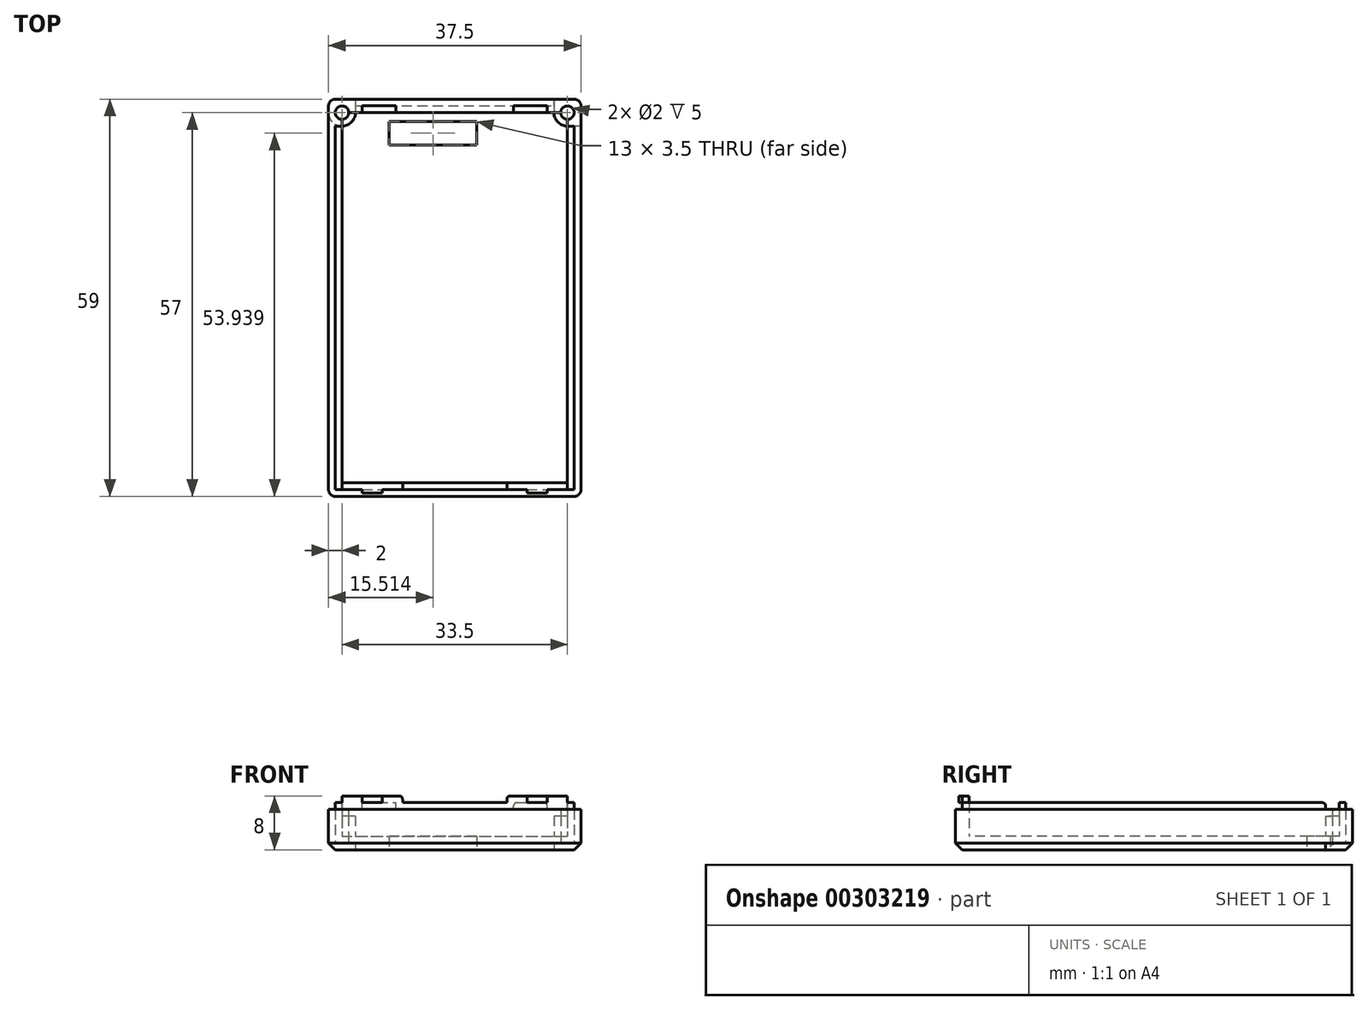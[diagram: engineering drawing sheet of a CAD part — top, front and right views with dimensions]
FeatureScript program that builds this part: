
annotation { "Feature Type Name" : "Feature", "Feature Type Description" : "" }
export const myFeature = defineFeature(function(context is Context, id is Id, definition is map)
    precondition{}
    {
        {
            var Q0;
            Q0=qCreatedBy(makeId("Top.planeOp"),FACE);
            var sketch = newSketch(context, id + "F0", { "sketchPlane" : qUnion([Q0])});
            skLineSegment(sketch, "E0.left", {"start": v(-18.5, 29.5) * mm, "end": v(-18.5, -29.5) * mm});
            skLineSegment(sketch, "E0.right", {"start": v(19, 29.5) * mm, "end": v(19, -29.5) * mm});
            skLineSegment(sketch, "E1", {"start": v(-18.5, 29.5) * mm, "end": v(-6.5, 29.5) * mm});
            skLineSegment(sketch, "E2", {"start": v(7, 29.5) * mm, "end": v(19, 29.5) * mm});
            skLineSegment(sketch, "E3", {"start": v(-18.5, -29.5) * mm, "end": v(-6.5, -29.5) * mm});
            skLineSegment(sketch, "E4", {"start": v(7, -29.5) * mm, "end": v(19, -29.5) * mm});
            skLineSegment(sketch, "E5", {"start": v(-6.5, 29.5) * mm, "end": v(7, 29.5) * mm});
            skLineSegment(sketch, "E6", {"start": v(-6.5, -29.5) * mm, "end": v(7, -29.5) * mm});
            skSolve(sketch);
        }
        {
            var Q0;
            Q0=makeQuery(id+"F0.imprint","IMPRINT",FACE,{"disambiguationData":[TD([[makeQuery(id+"F0.imprint","IMPRINT",EDGE,{"derivedFrom":sQuery(id+"F0.wireOp",EDGE,"E0.left")}),1.0]])]});
            extrude(context, id + "F1", {"entities" : qUnion([Q0]), "depth" : 6 * mm});
        }
        {
            var Q0;
            Q0=makeQuery(id+"F1.opExtrude","CAP_FACE",FACE,{"disambiguationData":[OSD([sQuery(id+"F0.wireOp",EDGE,"E0.left"),sQuery(id+"F0.wireOp",EDGE,"E0.right"),sQuery(id+"F0.wireOp",EDGE,"E1"),sQuery(id+"F0.wireOp",EDGE,"E2"),sQuery(id+"F0.wireOp",EDGE,"E3"),sQuery(id+"F0.wireOp",EDGE,"E4"),sQuery(id+"F0.wireOp",EDGE,"E5"),sQuery(id+"F0.wireOp",EDGE,"E6")])],"isStart":false});
            shell(context, id + "F2", {"entities" : qUnion([Q0]), "thickness" : 1 * mm});
        }
        {
            var Q0;
            Q0=makeQuery(id+"F2.opShell","OFFSET_FACE",FACE,{"disambiguationData":[OSD([sQuery(id+"F0.wireOp",EDGE,"E0.left"),sQuery(id+"F0.wireOp",EDGE,"E0.right"),sQuery(id+"F0.wireOp",EDGE,"E1"),sQuery(id+"F0.wireOp",EDGE,"E2"),sQuery(id+"F0.wireOp",EDGE,"E3"),sQuery(id+"F0.wireOp",EDGE,"E4"),sQuery(id+"F0.wireOp",EDGE,"E5"),sQuery(id+"F0.wireOp",EDGE,"E6")])]});
            extrude(context, id + "F3", {"entities" : qUnion([Q0]), "depth" : 6 * mm});
        }
        {
            var Q0;
            Q0=makeQuery(id+"F3.opExtrude","CAP_FACE",FACE,{"disambiguationData":[OSD([sQuery(id+"F0.wireOp",EDGE,"E0.left"),sQuery(id+"F0.wireOp",EDGE,"E0.right"),sQuery(id+"F0.wireOp",EDGE,"E1"),sQuery(id+"F0.wireOp",EDGE,"E2"),sQuery(id+"F0.wireOp",EDGE,"E3"),sQuery(id+"F0.wireOp",EDGE,"E4"),sQuery(id+"F0.wireOp",EDGE,"E5"),sQuery(id+"F0.wireOp",EDGE,"E6")])],"isStart":false});
            shell(context, id + "F4", {"entities" : qUnion([Q0]), "thickness" : 1 * mm});
        }
        {
            var Q0;
            Q0=makeQuery(id+"F1.opExtrude","CAP_FACE",FACE,{"disambiguationData":[OSD([sQuery(id+"F0.wireOp",EDGE,"E0.left"),sQuery(id+"F0.wireOp",EDGE,"E0.right"),sQuery(id+"F0.wireOp",EDGE,"E1"),sQuery(id+"F0.wireOp",EDGE,"E2"),sQuery(id+"F0.wireOp",EDGE,"E3"),sQuery(id+"F0.wireOp",EDGE,"E4"),sQuery(id+"F0.wireOp",EDGE,"E5"),sQuery(id+"F0.wireOp",EDGE,"E6")])],"isStart":true});
            var sketch = newSketch(context, id + "F5", { "sketchPlane" : qUnion([Q0])});
            skLineSegment(sketch, "E7", {"start": v(19, -29.5) * mm, "end": v(17, -29.5) * mm, "construction": true});
            skLineSegment(sketch, "E8", {"start": v(19, -29.5) * mm, "end": v(19, -27.5) * mm, "construction": true});
            skLineSegment(sketch, "E9", {"start": v(-18.5, -29.5) * mm, "end": v(-16.5, -29.5) * mm, "construction": true});
            skLineSegment(sketch, "E10", {"start": v(-18.5, -29.5) * mm, "end": v(-18.5, -27.5) * mm, "construction": true});
            skCircle(sketch, "E11", {"center": v(-16.5, -27.5) * mm, "radius": 2 * mm});
            skPoint(sketch, "E11.third.point", {"position": v(-15.03, -26.14) * mm});
            skCircle(sketch, "E12", {"center": v(17, -27.5) * mm, "radius": 2 * mm});
            skPoint(sketch, "E12.third.point", {"position": v(15.34, -26.38) * mm});
            skCircle(sketch, "E13", {"center": v(-16.5, -27.5) * mm, "radius": 1 * mm});
            skCircle(sketch, "E14", {"center": v(17, -27.5) * mm, "radius": 1 * mm});
            skSolve(sketch);
        }
        {
            var Q0;
            Q0=makeQuery(id+"F5.imprint","IMPRINT",FACE,{"disambiguationData":[TD([[makeQuery(id+"F5.imprint","IMPRINT",EDGE,{"derivedFrom":sQuery(id+"F5.wireOp",EDGE,"E14")}),-1.0]])]});
            var Q1;
            Q1=makeQuery(id+"F5.imprint","IMPRINT",FACE,{"disambiguationData":[TD([[makeQuery(id+"F5.imprint","IMPRINT",EDGE,{"derivedFrom":sQuery(id+"F5.wireOp",EDGE,"E13")}),-1.0]])]});
            extrude(context, id + "F6", {"entities" : qUnion([Q0, Q1]), "operationType" : NewBodyOperationType.ADD, "oppositeDirection" : true, "depth" : 5 * mm});
        }
        {
            var Q0;
            Q0=makeQuery(id+"F3.opExtrude","CAP_FACE",FACE,{"disambiguationData":[OSD([sQuery(id+"F0.wireOp",EDGE,"E0.left"),sQuery(id+"F0.wireOp",EDGE,"E0.right"),sQuery(id+"F0.wireOp",EDGE,"E1"),sQuery(id+"F0.wireOp",EDGE,"E2"),sQuery(id+"F0.wireOp",EDGE,"E3"),sQuery(id+"F0.wireOp",EDGE,"E4"),sQuery(id+"F0.wireOp",EDGE,"E5"),sQuery(id+"F0.wireOp",EDGE,"E6")])],"isStart":false});
            var sketch = newSketch(context, id + "F7", { "sketchPlane" : qUnion([Q0])});
            skLineSegment(sketch, "E15", {"start": v(-17.5, 28.5) * mm, "end": v(-17.5, 25.5) * mm});
            skLineSegment(sketch, "E16", {"start": v(-17.5, 25.5) * mm, "end": v(-16.5, 25.5) * mm});
            skLineSegment(sketch, "E17", {"start": v(-16.5, 25.5) * mm, "end": v(-16.5, 27.5) * mm});
            skLineSegment(sketch, "E18", {"start": v(-16.5, 27.5) * mm, "end": v(-13.5, 27.5) * mm});
            skLineSegment(sketch, "E19", {"start": v(-13.5, 27.5) * mm, "end": v(-13.5, 28.5) * mm});
            skLineSegment(sketch, "E20", {"start": v(-13.5, 28.5) * mm, "end": v(-17.5, 28.5) * mm});
            skLineSegment(sketch, "E21", {"start": v(17, 27.5) * mm, "end": v(14, 27.5) * mm});
            skLineSegment(sketch, "E22", {"start": v(14, 27.5) * mm, "end": v(14, 28.5) * mm});
            skLineSegment(sketch, "E23", {"start": v(14, 28.5) * mm, "end": v(18, 28.5) * mm});
            skLineSegment(sketch, "E24", {"start": v(18, 28.5) * mm, "end": v(18, 25.5) * mm});
            skLineSegment(sketch, "E25", {"start": v(18, 25.5) * mm, "end": v(17, 25.5) * mm});
            skLineSegment(sketch, "E26", {"start": v(17, 25.5) * mm, "end": v(17, 27.5) * mm});
            skLineSegment(sketch, "E27", {"start": v(-13.5, 28.5) * mm, "end": v(-8.5, 28.5) * mm, "construction": true});
            skLineSegment(sketch, "E28", {"start": v(-8.5, 28.5) * mm, "end": v(9, 28.5) * mm});
            skLineSegment(sketch, "E29", {"start": v(9, 28.5) * mm, "end": v(14, 28.5) * mm, "construction": true});
            skLineSegment(sketch, "E30", {"start": v(-13.5, 27.5) * mm, "end": v(-8.5, 27.5) * mm, "construction": true});
            skLineSegment(sketch, "E31", {"start": v(-8.5, 27.5) * mm, "end": v(9, 27.5) * mm});
            skLineSegment(sketch, "E32", {"start": v(9, 27.5) * mm, "end": v(14, 27.5) * mm, "construction": true});
            skLineSegment(sketch, "E33", {"start": v(9, 28.5) * mm, "end": v(9, 27.5) * mm});
            skLineSegment(sketch, "E34", {"start": v(-8.5, 28.5) * mm, "end": v(-8.5, 27.5) * mm});
            skSolve(sketch);
        }
        {
            var Q0;
            Q0=makeQuery(id+"F7.imprint","IMPRINT",FACE,{"disambiguationData":[TD([[makeQuery(id+"F7.imprint","IMPRINT",EDGE,{"derivedFrom":sQuery(id+"F7.wireOp",EDGE,"E15")}),1.0]])]});
            var Q1;
            Q1=makeQuery(id+"F7.imprint","IMPRINT",FACE,{"disambiguationData":[TD([[makeQuery(id+"F7.imprint","IMPRINT",EDGE,{"derivedFrom":sQuery(id+"F7.wireOp",EDGE,"E21")}),1.0]])]});
            var Q2;
            Q2=makeQuery(id+"F7.imprint","IMPRINT",FACE,{"disambiguationData":[TD([[makeQuery(id+"F7.imprint","IMPRINT",EDGE,{"derivedFrom":sQuery(id+"F7.wireOp",EDGE,"E28")}),-1.0]])]});
            extrude(context, id + "F8", {"entities" : qUnion([Q0, Q1, Q2]), "operationType" : NewBodyOperationType.REMOVE, "oppositeDirection" : true, "depth" : 1 * mm});
        }
        {
            var Q0;
            Q0=makeQuery(id+"F5.imprint","IMPRINT",FACE,{"disambiguationData":[TD([[makeQuery(id+"F5.imprint","IMPRINT",EDGE,{"derivedFrom":sQuery(id+"F5.wireOp",EDGE,"E13")}),1.0]])]});
            var Q1;
            Q1=makeQuery(id+"F5.imprint","IMPRINT",FACE,{"disambiguationData":[TD([[makeQuery(id+"F5.imprint","IMPRINT",EDGE,{"derivedFrom":sQuery(id+"F5.wireOp",EDGE,"E14")}),1.0]])]});
            extrude(context, id + "F9", {"entities" : qUnion([Q0, Q1]), "operationType" : NewBodyOperationType.REMOVE, "oppositeDirection" : true, "depth" : 7 * mm});
        }
        {
            var Q0;
            {var subQ0=sQuery(id+"F0.wireOp",EDGE,"E6");var subQ1=sQuery(id+"F0.wireOp",EDGE,"E4");var subQ2=sQuery(id+"F0.wireOp",EDGE,"E3");var subQ3=sQuery(id+"F0.wireOp",EDGE,"E0.left");var subQ4=sQuery(id+"F0.wireOp",EDGE,"E0.right");Q0=makeQuery(id+"F8.boolean.opBoolean","SPLIT",FACE,{"disambiguationData":[TD([makeQuery(id+"F3.opExtrude","SWEPT_FACE",FACE,{"disambiguationData":[OSD([subQ3])]})])],"derivedFrom":makeQuery(id+"F3.opExtrude","CAP_FACE",FACE,{"disambiguationData":[OSD([subQ3,subQ4,sQuery(id+"F0.wireOp",EDGE,"E1"),sQuery(id+"F0.wireOp",EDGE,"E2"),subQ2,subQ1,sQuery(id+"F0.wireOp",EDGE,"E5"),subQ0])],"isStart":false})});}
            var sketch = newSketch(context, id + "F10", { "sketchPlane" : qUnion([Q0])});
            skLineSegment(sketch, "E35", {"start": v(17, -27.5) * mm, "end": v(18, -27.5) * mm, "construction": true});
            skLineSegment(sketch, "E36", {"start": v(18, -27.5) * mm, "end": v(18, -28.5) * mm, "construction": true});
            skLineSegment(sketch, "E37", {"start": v(18, -28.5) * mm, "end": v(17, -28.5) * mm, "construction": true});
            skLineSegment(sketch, "E38", {"start": v(17, -28.5) * mm, "end": v(8, -28.5) * mm});
            skLineSegment(sketch, "E39", {"start": v(8, -28.5) * mm, "end": v(8, -27.5) * mm});
            skLineSegment(sketch, "E40", {"start": v(8, -27.5) * mm, "end": v(17, -27.5) * mm});
            skLineSegment(sketch, "E41", {"start": v(17, -27.5) * mm, "end": v(17, -28.5) * mm});
            skLineSegment(sketch, "E42", {"start": v(-17.5, -27.5) * mm, "end": v(-16.5, -27.5) * mm, "construction": true});
            skLineSegment(sketch, "E43", {"start": v(-16.5, -27.5) * mm, "end": v(-16.5, -28.5) * mm});
            skLineSegment(sketch, "E44", {"start": v(-16.5, -28.5) * mm, "end": v(-7.5, -28.5) * mm});
            skLineSegment(sketch, "E45", {"start": v(-7.5, -28.5) * mm, "end": v(-7.5, -27.5) * mm});
            skLineSegment(sketch, "E46", {"start": v(-7.5, -27.5) * mm, "end": v(-16.5, -27.5) * mm});
            skLineSegment(sketch, "E47", {"start": v(-17.5, -27.5) * mm, "end": v(-17.5, -28.5) * mm, "construction": true});
            skLineSegment(sketch, "E48", {"start": v(-17.5, -28.5) * mm, "end": v(-16.5, -28.5) * mm, "construction": true});
            skSolve(sketch);
        }
        {
            var Q0;
            Q0=makeQuery(id+"F10.imprint","IMPRINT",FACE,{"disambiguationData":[TD([[makeQuery(id+"F10.imprint","IMPRINT",EDGE,{"derivedFrom":sQuery(id+"F10.wireOp",EDGE,"E43")}),1.0]])]});
            var Q1;
            Q1=makeQuery(id+"F10.imprint","IMPRINT",FACE,{"disambiguationData":[TD([[makeQuery(id+"F10.imprint","IMPRINT",EDGE,{"derivedFrom":sQuery(id+"F10.wireOp",EDGE,"E38")}),1.0]])]});
            extrude(context, id + "F11", {"entities" : qUnion([Q0, Q1]), "operationType" : NewBodyOperationType.ADD, "depth" : 1 * mm});
        }
        {
            var Q0;
            Q0=makeQuery(id+"F8.boolean.opBoolean","COPY",EDGE,{"derivedFrom":makeQuery(id+"F8.opExtrude","CAP_EDGE",EDGE,{"disambiguationData":[OSD([sQuery(id+"F7.wireOp",EDGE,"E34")])],"isStart":true})});
            var Q1;
            Q1=makeQuery(id+"F8.boolean.opBoolean","COPY",EDGE,{"derivedFrom":makeQuery(id+"F8.opExtrude","CAP_EDGE",EDGE,{"disambiguationData":[OSD([sQuery(id+"F7.wireOp",EDGE,"E19")])],"isStart":true})});
            var Q2;
            Q2=makeQuery(id+"F8.boolean.opBoolean","COPY",EDGE,{"derivedFrom":makeQuery(id+"F8.opExtrude","CAP_EDGE",EDGE,{"disambiguationData":[OSD([sQuery(id+"F7.wireOp",EDGE,"E22")])],"isStart":true})});
            var Q3;
            Q3=makeQuery(id+"F8.boolean.opBoolean","COPY",EDGE,{"derivedFrom":makeQuery(id+"F8.opExtrude","CAP_EDGE",EDGE,{"disambiguationData":[OSD([sQuery(id+"F7.wireOp",EDGE,"E33")])],"isStart":true})});
            var Q4;
            Q4=makeQuery(id+"F8.boolean.opBoolean","COPY",EDGE,{"derivedFrom":makeQuery(id+"F8.opExtrude","CAP_EDGE",EDGE,{"disambiguationData":[OSD([sQuery(id+"F7.wireOp",EDGE,"E25")])],"isStart":true})});
            var Q5;
            Q5=makeQuery(id+"F8.boolean.opBoolean","COPY",EDGE,{"derivedFrom":makeQuery(id+"F8.opExtrude","CAP_EDGE",EDGE,{"disambiguationData":[OSD([sQuery(id+"F7.wireOp",EDGE,"E16")])],"isStart":true})});
            var Q6;
            Q6=makeQuery(id+"F11.opExtrude","CAP_EDGE",EDGE,{"disambiguationData":[OSD([sQuery(id+"F10.wireOp",EDGE,"E45")])],"isStart":false});
            var Q7;
            Q7=makeQuery(id+"F11.opExtrude","CAP_EDGE",EDGE,{"disambiguationData":[OSD([sQuery(id+"F10.wireOp",EDGE,"E39")])],"isStart":false});
            fillet(context, id + "F12", {"entities" : qUnion([Q0, Q1, Q2, Q3, Q4, Q5, Q6, Q7]), "radius" : 0.5 * mm, "tangentPropagation" : true, "allowEdgeOverflow" : false});
        }
        {
            var Q0;
            Q0=makeQuery(id+"F11.boolean.opBoolean","MERGE",FACE,{"derivedFrom":[makeQuery(id+"F3.opExtrude","SWEPT_FACE",FACE,{"disambiguationData":[OSD([sQuery(id+"F0.wireOp",EDGE,"E3"),sQuery(id+"F0.wireOp",EDGE,"E4"),sQuery(id+"F0.wireOp",EDGE,"E6")])]}),makeQuery(id+"F11.opExtrude","SWEPT_FACE",FACE,{"disambiguationData":[OSD([sQuery(id+"F10.wireOp",EDGE,"E38")])]}),makeQuery(id+"F11.opExtrude","SWEPT_FACE",FACE,{"disambiguationData":[OSD([sQuery(id+"F10.wireOp",EDGE,"E44")])]})]});
            var sketch = newSketch(context, id + "F13", { "sketchPlane" : qUnion([Q0])});
            skLineSegment(sketch, "E49", {"start": v(17, 8) * mm, "end": v(14, 8) * mm, "construction": true});
            skLineSegment(sketch, "E50", {"start": v(14, 8) * mm, "end": v(11, 8) * mm});
            skLineSegment(sketch, "E51", {"start": v(11, 8) * mm, "end": v(8, 8) * mm, "construction": true});
            skLineSegment(sketch, "E52", {"start": v(8, 8) * mm, "end": v(8, 7) * mm, "construction": true});
            skLineSegment(sketch, "E53", {"start": v(8, 7) * mm, "end": v(11, 7) * mm, "construction": true});
            skLineSegment(sketch, "E54", {"start": v(11, 7) * mm, "end": v(14, 7) * mm});
            skLineSegment(sketch, "E55", {"start": v(14, 7) * mm, "end": v(17, 7) * mm, "construction": true});
            skLineSegment(sketch, "E56", {"start": v(17, 7) * mm, "end": v(17, 8) * mm, "construction": true});
            skLineSegment(sketch, "E57", {"start": v(14, 8) * mm, "end": v(14, 7) * mm});
            skLineSegment(sketch, "E58", {"start": v(11, 8) * mm, "end": v(11, 7) * mm});
            skLineSegment(sketch, "E59", {"start": v(-13.5, 8) * mm, "end": v(-10.5, 8) * mm});
            skLineSegment(sketch, "E60", {"start": v(-10.5, 8) * mm, "end": v(-7.5, 8) * mm, "construction": true});
            skLineSegment(sketch, "E61", {"start": v(-16.5, 8) * mm, "end": v(-13.5, 8) * mm, "construction": true});
            skLineSegment(sketch, "E62", {"start": v(-16.5, 8) * mm, "end": v(-16.5, 7) * mm, "construction": true});
            skLineSegment(sketch, "E63", {"start": v(-16.5, 7) * mm, "end": v(-13.5, 7) * mm, "construction": true});
            skLineSegment(sketch, "E64", {"start": v(-13.5, 7) * mm, "end": v(-10.5, 7) * mm});
            skLineSegment(sketch, "E65", {"start": v(-10.5, 7) * mm, "end": v(-7.5, 7) * mm, "construction": true});
            skLineSegment(sketch, "E66", {"start": v(-7.5, 8) * mm, "end": v(-7.5, 7) * mm, "construction": true});
            skLineSegment(sketch, "E67", {"start": v(-10.5, 8) * mm, "end": v(-10.5, 7) * mm});
            skLineSegment(sketch, "E68", {"start": v(-13.5, 8) * mm, "end": v(-13.5, 7) * mm});
            skSolve(sketch);
        }
        {
            var Q0;
            Q0=makeQuery(id+"F13.imprint","IMPRINT",FACE,{"disambiguationData":[TD([[makeQuery(id+"F13.imprint","IMPRINT",EDGE,{"derivedFrom":sQuery(id+"F13.wireOp",EDGE,"E59")}),-1.0]])]});
            var Q1;
            Q1=makeQuery(id+"F13.imprint","IMPRINT",FACE,{"disambiguationData":[TD([[makeQuery(id+"F13.imprint","IMPRINT",EDGE,{"derivedFrom":sQuery(id+"F13.wireOp",EDGE,"E50")}),-1.0]])]});
            extrude(context, id + "F14", {"entities" : qUnion([Q0, Q1]), "operationType" : NewBodyOperationType.ADD, "depth" : 0.5 * mm});
        }
        {
            var Q0;
            {var subQ0=makeQuery(id+"F1.opExtrude","CAP_EDGE",EDGE,{"disambiguationData":[OSD([sQuery(id+"F0.wireOp",EDGE,"E3"),sQuery(id+"F0.wireOp",EDGE,"E4"),sQuery(id+"F0.wireOp",EDGE,"E6")])],"isStart":true});Q0=makeQuery(id+"F5.imprint","IMPRINT",FACE,{"disambiguationData":[TD([[makeQuery(id+"F5.imprint","IMPRINT",EDGE,{"derivedFrom":subQ0}),-1.0]])]});}
            var sketch = newSketch(context, id + "F15", { "sketchPlane" : qUnion([Q0])});
            skLineSegment(sketch, "E69", {"start": v(29.42, 27.62) * mm, "end": v(27.42, 27.62) * mm, "construction": true});
            skLineSegment(sketch, "E70", {"start": v(29.42, 27.62) * mm, "end": v(29.42, 29.62) * mm, "construction": true});
            skLineSegment(sketch, "E71", {"start": v(-7.58, 27.62) * mm, "end": v(-5.58, 27.62) * mm, "construction": true});
            skLineSegment(sketch, "E72", {"start": v(-7.58, 27.62) * mm, "end": v(-7.58, 29.62) * mm, "construction": true});
            skCircle(sketch, "E73", {"center": v(-5.58, 29.62) * mm, "radius": 2 * mm});
            skPoint(sketch, "E73.third.point", {"position": v(-4.11, 30.98) * mm});
            skCircle(sketch, "E74", {"center": v(27.42, 29.62) * mm, "radius": 2 * mm});
            skPoint(sketch, "E74.third.point", {"position": v(25.76, 30.74) * mm});
            skCircle(sketch, "E75", {"center": v(-5.58, 29.62) * mm, "radius": 1 * mm});
            skCircle(sketch, "E76", {"center": v(27.42, 29.62) * mm, "radius": 1 * mm});
            skCircle(sketch, "E77", {"center": v(17, -27.5) * mm, "radius": 2 * mm});
            skLineSegment(sketch, "E78", {"start": v(19, -29.5) * mm, "end": v(19, -25.5) * mm});
            skLineSegment(sketch, "E79", {"start": v(15, -29.5) * mm, "end": v(19, -29.5) * mm});
            skPoint(sketch, "E80.endSnap0", {"position": v(15, -27.5) * mm});
            skLineSegment(sketch, "E81", {"start": v(19, -25.5) * mm, "end": v(17, -25.5) * mm});
            skLineSegment(sketch, "E82", {"start": v(17, -25.5) * mm, "end": v(15, -25.5) * mm, "construction": true});
            skLineSegment(sketch, "E83", {"start": v(15, -25.5) * mm, "end": v(15, -27.5) * mm, "construction": true});
            skLineSegment(sketch, "E84", {"start": v(15, -29.5) * mm, "end": v(15, -27.5) * mm});
            skCircle(sketch, "E85", {"center": v(-16.5, -27.5) * mm, "radius": 2 * mm});
            skLineSegment(sketch, "E86", {"start": v(-18.5, -29.5) * mm, "end": v(-16.5, -29.5) * mm});
            skLineSegment(sketch, "E87", {"start": v(-16.5, -29.5) * mm, "end": v(-14.5, -29.5) * mm});
            skLineSegment(sketch, "E88", {"start": v(-14.5, -29.5) * mm, "end": v(-14.5, -27.5) * mm});
            skLineSegment(sketch, "E89", {"start": v(-14.5, -27.5) * mm, "end": v(-14.5, -25.5) * mm, "construction": true});
            skLineSegment(sketch, "E90", {"start": v(-14.5, -25.5) * mm, "end": v(-16.53, -25.5) * mm, "construction": true});
            skLineSegment(sketch, "E91", {"start": v(-16.53, -25.5) * mm, "end": v(-18.5, -25.5) * mm});
            skLineSegment(sketch, "E92", {"start": v(-18.5, -25.5) * mm, "end": v(-18.5, -27.5) * mm});
            skLineSegment(sketch, "E93", {"start": v(-18.5, -27.5) * mm, "end": v(-18.5, -29.5) * mm});
            skSolve(sketch);
        }
        {
            var Q0;
            Q0=makeQuery(id+"F5.imprint","IMPRINT",FACE,{"disambiguationData":[TD([[makeQuery(id+"F5.imprint","IMPRINT",EDGE,{"derivedFrom":sQuery(id+"F5.wireOp",EDGE,"E13")}),-1.0]])]});
            var Q1;
            {var subQ0=sQuery(id+"F15.wireOp",EDGE,"E85");var subQ4=sQuery(id+"F15.wireOp",EDGE,"E91");var subQ5=makeQuery(id+"F15.imprint","INTERSECT",VERTEX,{"derivedFrom":[subQ0,subQ4]});Q1=makeQuery(id+"F15.imprint","IMPRINT",FACE,{"disambiguationData":[TD([[makeQuery(id+"F15.imprint","IMPRINT",EDGE,{"disambiguationData":[TD([[subQ5,-1.0]])],"derivedFrom":subQ4}),1.0]])]});}
            var Q2;
            {var subQ0=sQuery(id+"F15.wireOp",EDGE,"E86");Q2=makeQuery(id+"F15.imprint","IMPRINT",FACE,{"disambiguationData":[TD([[makeQuery(id+"F15.imprint","IMPRINT",EDGE,{"derivedFrom":subQ0}),1.0]])]});}
            var Q3;
            {var subQ0=sQuery(id+"F15.wireOp",EDGE,"E87");Q3=makeQuery(id+"F15.imprint","IMPRINT",FACE,{"disambiguationData":[TD([[makeQuery(id+"F15.imprint","IMPRINT",EDGE,{"derivedFrom":subQ0}),1.0]])]});}
            var Q4;
            Q4=makeQuery(id+"F5.imprint","IMPRINT",FACE,{"disambiguationData":[TD([[makeQuery(id+"F5.imprint","IMPRINT",EDGE,{"derivedFrom":sQuery(id+"F5.wireOp",EDGE,"E14")}),-1.0]])]});
            var Q5;
            {var subQ3=sQuery(id+"F15.wireOp",EDGE,"E84");Q5=makeQuery(id+"F15.imprint","IMPRINT",FACE,{"disambiguationData":[TD([[makeQuery(id+"F15.imprint","IMPRINT",EDGE,{"derivedFrom":subQ3}),-1.0]])]});}
            var Q6;
            {var subQ0=sQuery(id+"F15.wireOp",EDGE,"E78");var subQ1=sQuery(id+"F15.wireOp",EDGE,"E77");var subQ2=makeQuery(id+"F15.imprint","INTERSECT",VERTEX,{"derivedFrom":[subQ1,subQ0]});Q6=makeQuery(id+"F15.imprint","IMPRINT",FACE,{"disambiguationData":[TD([[makeQuery(id+"F15.imprint","IMPRINT",EDGE,{"disambiguationData":[TD([[subQ2,1.0]])],"derivedFrom":subQ1}),-1.0]])]});}
            var Q7;
            {var subQ3=sQuery(id+"F15.wireOp",EDGE,"E81");Q7=makeQuery(id+"F15.imprint","IMPRINT",FACE,{"disambiguationData":[TD([[makeQuery(id+"F15.imprint","IMPRINT",EDGE,{"derivedFrom":subQ3}),1.0]])]});}
            extrude(context, id + "F16", {"entities" : qUnion([Q0, Q1, Q2, Q3, Q4, Q5, Q6, Q7]), "operationType" : NewBodyOperationType.REMOVE, "oppositeDirection" : true, "depth" : 1 * mm});
        }
        {
            var Q0;
            Q0=makeQuery(id+"F1.opExtrude","SWEPT_EDGE",EDGE,{"disambiguationData":[OSD([sQuery(id+"F0.wireOp",EDGE,"E0.left"),sQuery(id+"F0.wireOp",EDGE,"E1")])]});
            var Q1;
            Q1=makeQuery(id+"F1.opExtrude","SWEPT_EDGE",EDGE,{"disambiguationData":[OSD([sQuery(id+"F0.wireOp",EDGE,"E0.left"),sQuery(id+"F0.wireOp",EDGE,"E3")])]});
            var Q2;
            Q2=makeQuery(id+"F1.opExtrude","SWEPT_EDGE",EDGE,{"disambiguationData":[OSD([sQuery(id+"F0.wireOp",EDGE,"E0.right"),sQuery(id+"F0.wireOp",EDGE,"E4")])]});
            var Q3;
            Q3=makeQuery(id+"F1.opExtrude","SWEPT_EDGE",EDGE,{"disambiguationData":[OSD([sQuery(id+"F0.wireOp",EDGE,"E0.right"),sQuery(id+"F0.wireOp",EDGE,"E2")])]});
            fillet(context, id + "F17", {"entities" : qUnion([Q0, Q1, Q2, Q3]), "radius" : 1 * mm, "tangentPropagation" : true, "allowEdgeOverflow" : false});
        }
        {
            var Q0;
            Q0=makeQuery(id+"F1.opExtrude","CAP_EDGE",EDGE,{"disambiguationData":[OSD([sQuery(id+"F0.wireOp",EDGE,"E1"),sQuery(id+"F0.wireOp",EDGE,"E2"),sQuery(id+"F0.wireOp",EDGE,"E5")])],"isStart":true});
            var Q1;
            Q1=makeQuery(id+"F1.opExtrude","CAP_EDGE",EDGE,{"disambiguationData":[OSD([sQuery(id+"F0.wireOp",EDGE,"E0.right")])],"isStart":true});
            var Q2;
            Q2=makeQuery(id+"F1.opExtrude","CAP_EDGE",EDGE,{"disambiguationData":[OSD([sQuery(id+"F0.wireOp",EDGE,"E3"),sQuery(id+"F0.wireOp",EDGE,"E4"),sQuery(id+"F0.wireOp",EDGE,"E6")])],"isStart":true});
            var Q3;
            Q3=makeQuery(id+"F1.opExtrude","CAP_EDGE",EDGE,{"disambiguationData":[OSD([sQuery(id+"F0.wireOp",EDGE,"E0.left")])],"isStart":true});
            var Q4;
            {var subQ0=sQuery(id+"F0.wireOp",EDGE,"E4");var subQ1=sQuery(id+"F0.wireOp",EDGE,"E0.right");Q4=makeQuery(id+"F17.opFillet","BLEND_EDGE",EDGE,{"blendedFrom":[makeQuery(id+"F1.opExtrude","SWEPT_EDGE",EDGE,{"disambiguationData":[OSD([subQ1,subQ0])]}),makeQuery(id+"F1.opExtrude","CAP_FACE",FACE,{"disambiguationData":[OSD([sQuery(id+"F0.wireOp",EDGE,"E0.left"),subQ1,sQuery(id+"F0.wireOp",EDGE,"E1"),sQuery(id+"F0.wireOp",EDGE,"E2"),sQuery(id+"F0.wireOp",EDGE,"E3"),subQ0,sQuery(id+"F0.wireOp",EDGE,"E5"),sQuery(id+"F0.wireOp",EDGE,"E6")])],"isStart":true})],"blendedInto":[makeQuery(id+"F1.opExtrude","CAP_FACE",FACE,{"disambiguationData":[OSD([sQuery(id+"F0.wireOp",EDGE,"E0.left"),subQ1,sQuery(id+"F0.wireOp",EDGE,"E1"),sQuery(id+"F0.wireOp",EDGE,"E2"),sQuery(id+"F0.wireOp",EDGE,"E3"),subQ0,sQuery(id+"F0.wireOp",EDGE,"E5"),sQuery(id+"F0.wireOp",EDGE,"E6")])],"isStart":true})]});}
            var Q5;
            {var subQ0=sQuery(id+"F0.wireOp",EDGE,"E3");var subQ1=sQuery(id+"F0.wireOp",EDGE,"E0.left");Q5=makeQuery(id+"F17.opFillet","BLEND_EDGE",EDGE,{"blendedFrom":[makeQuery(id+"F1.opExtrude","SWEPT_EDGE",EDGE,{"disambiguationData":[OSD([subQ1,subQ0])]}),makeQuery(id+"F1.opExtrude","CAP_FACE",FACE,{"disambiguationData":[OSD([subQ1,sQuery(id+"F0.wireOp",EDGE,"E0.right"),sQuery(id+"F0.wireOp",EDGE,"E1"),sQuery(id+"F0.wireOp",EDGE,"E2"),subQ0,sQuery(id+"F0.wireOp",EDGE,"E4"),sQuery(id+"F0.wireOp",EDGE,"E5"),sQuery(id+"F0.wireOp",EDGE,"E6")])],"isStart":true})],"blendedInto":[makeQuery(id+"F1.opExtrude","CAP_FACE",FACE,{"disambiguationData":[OSD([subQ1,sQuery(id+"F0.wireOp",EDGE,"E0.right"),sQuery(id+"F0.wireOp",EDGE,"E1"),sQuery(id+"F0.wireOp",EDGE,"E2"),subQ0,sQuery(id+"F0.wireOp",EDGE,"E4"),sQuery(id+"F0.wireOp",EDGE,"E5"),sQuery(id+"F0.wireOp",EDGE,"E6")])],"isStart":true})]});}
            chamfer(context, id + "F18", {"entities" : qUnion([Q0, Q1, Q2, Q3, Q4, Q5]), "width" : 1 * mm, "tangentPropagation" : true});
        }
        {
            var Q0;
            {var subQ0=makeQuery(id+"F1.opExtrude","CAP_EDGE",EDGE,{"disambiguationData":[OSD([sQuery(id+"F0.wireOp",EDGE,"E3"),sQuery(id+"F0.wireOp",EDGE,"E4"),sQuery(id+"F0.wireOp",EDGE,"E6")])],"isStart":true});Q0=makeQuery(id+"F5.imprint","IMPRINT",FACE,{"disambiguationData":[TD([[makeQuery(id+"F5.imprint","IMPRINT",EDGE,{"derivedFrom":subQ0}),-1.0]])]});}
            var sketch = newSketch(context, id + "F19", { "sketchPlane" : qUnion([Q0])});
            skLineSegment(sketch, "E94", {"start": v(-18.49, -29.49) * mm, "end": v(-18.49, -26.19) * mm, "construction": true});
            skLineSegment(sketch, "E95", {"start": v(-18.49, -26.19) * mm, "end": v(-9.49, -26.19) * mm, "construction": true});
            skLineSegment(sketch, "E96", {"start": v(-9.49, -26.19) * mm, "end": v(3.51, -26.19) * mm});
            skLineSegment(sketch, "E97", {"start": v(3.51, -22.69) * mm, "end": v(-9.49, -22.69) * mm});
            skLineSegment(sketch, "E98", {"start": v(-9.49, -22.69) * mm, "end": v(-9.49, -26.19) * mm});
            skLineSegment(sketch, "E99", {"start": v(3.51, -26.19) * mm, "end": v(3.51, -22.69) * mm});
            skSolve(sketch);
        }
        {
            var Q0;
            Q0=makeQuery(id+"F19.imprint","IMPRINT",FACE,{"disambiguationData":[TD([[makeQuery(id+"F19.imprint","IMPRINT",EDGE,{"derivedFrom":sQuery(id+"F19.wireOp",EDGE,"E96")}),1.0]])]});
            extrude(context, id + "F20", {"entities" : qUnion([Q0]), "operationType" : NewBodyOperationType.REMOVE, "oppositeDirection" : true, "depth" : 2 * mm});
        }
    });
